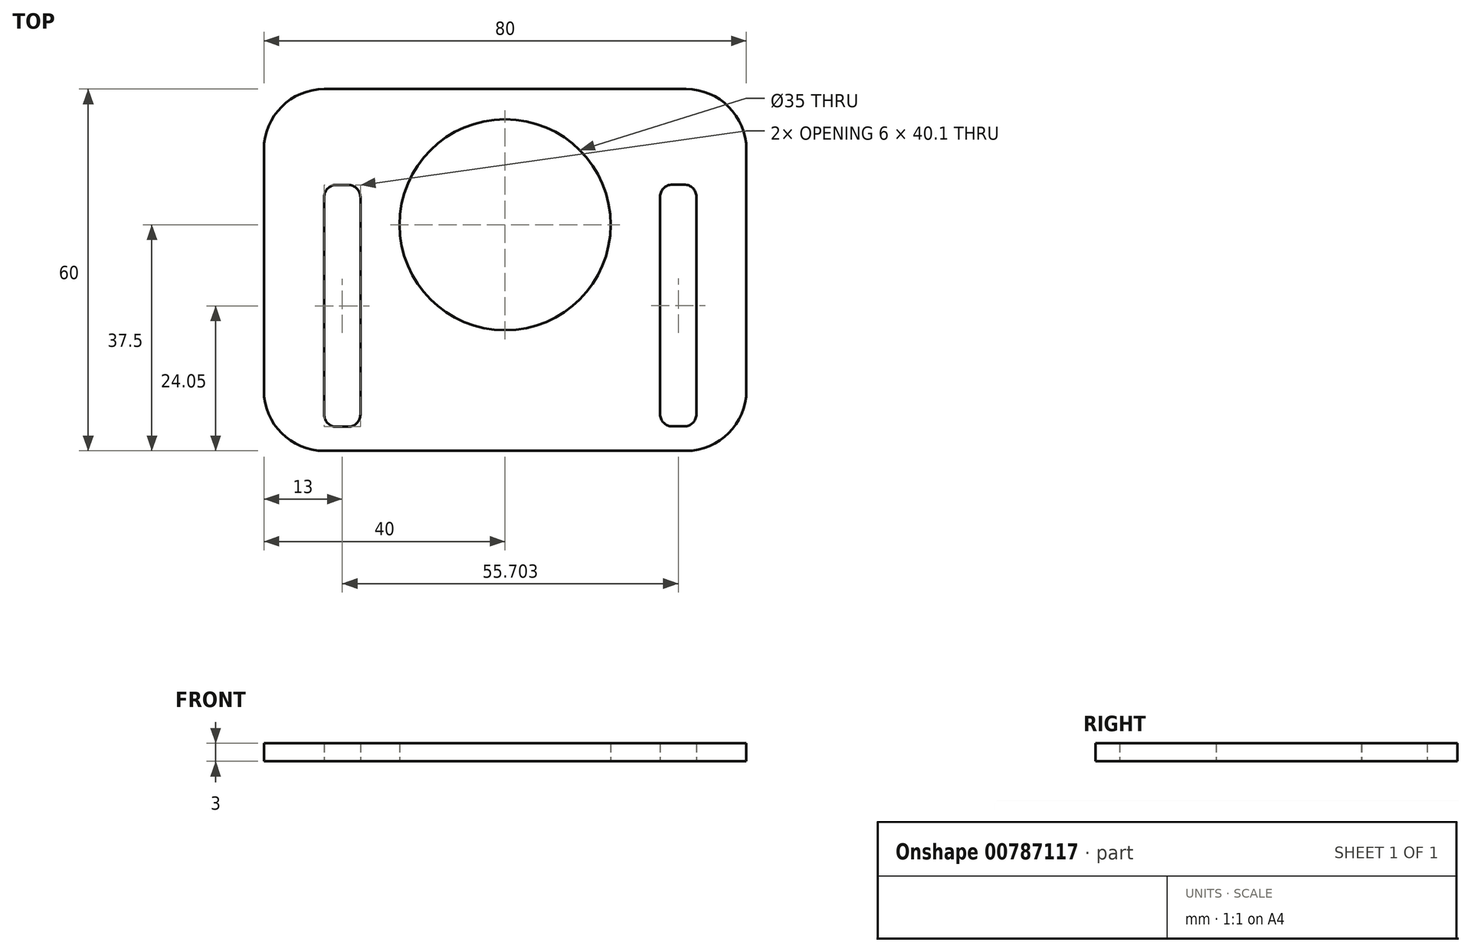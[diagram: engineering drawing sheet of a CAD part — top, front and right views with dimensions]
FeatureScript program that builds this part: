
annotation { "Feature Type Name" : "Feature", "Feature Type Description" : "" }
export const myFeature = defineFeature(function(context is Context, id is Id, definition is map)
    precondition{}
    {
        {
            var Q0;
            Q0=qCreatedBy(makeId("Top.planeOp"),FACE);
            var sketch = newSketch(context, id + "F0", { "sketchPlane" : qUnion([Q0])});
            skLineSegment(sketch, "E0.bottom", {"start": v(-10, 0) * mm, "end": v(-70, 0) * mm});
            skLineSegment(sketch, "E0.top", {"start": v(-10, 60) * mm, "end": v(-70, 60) * mm});
            skLineSegment(sketch, "E0.left", {"start": v(0, 10) * mm, "end": v(0, 50) * mm});
            skLineSegment(sketch, "E0.right", {"start": v(-80, 10) * mm, "end": v(-80, 50) * mm});
            skPoint(sketch, "E1.visualSharp", {"position": v(-80, 60) * mm});
            skArc(sketch, "E1.filletArc", {"start": v(-70, 60) * mm, "mid": v(-77.07, 57.07) * mm, "end": v(-80, 50) * mm});
            skPoint(sketch, "E2.visualSharp", {"position": v(0, 60) * mm});
            skArc(sketch, "E2.filletArc", {"start": v(0, 50) * mm, "mid": v(-2.93, 57.07) * mm, "end": v(-10, 60) * mm});
            skPoint(sketch, "E3.visualSharp", {"position": v(-80, 0) * mm});
            skArc(sketch, "E3.filletArc", {"start": v(-80, 10) * mm, "mid": v(-77.07, 2.93) * mm, "end": v(-70, 0) * mm});
            skPoint(sketch, "E4.visualSharp", {"position": v(0, 0) * mm});
            skArc(sketch, "E4.filletArc", {"start": v(-10, 0) * mm, "mid": v(-2.93, 2.93) * mm, "end": v(0, 10) * mm});
            skLineSegment(sketch, "E5", {"start": v(-40, 60) * mm, "end": v(-40, 55) * mm});
            skCircle(sketch, "E6", {"center": v(-40, 37.5) * mm, "radius": 17.5 * mm});
            skLineSegment(sketch, "E7", {"start": v(-70, 0) * mm, "end": v(-70, 4) * mm});
            skLineSegment(sketch, "E8", {"start": v(-80, 36.22) * mm, "end": v(-70.21, 36.22) * mm});
            skLineSegment(sketch, "E9.bottom", {"start": v(-68, 4) * mm, "end": v(-66, 4) * mm});
            skLineSegment(sketch, "E9.top", {"start": v(-68, 44.1) * mm, "end": v(-66, 44.1) * mm});
            skLineSegment(sketch, "E9.left", {"start": v(-70, 6) * mm, "end": v(-70, 42.1) * mm});
            skLineSegment(sketch, "E9.right", {"start": v(-64, 6) * mm, "end": v(-64, 42.1) * mm});
            skLineSegment(sketch, "E10.bottom", {"start": v(-12.3, 4.06) * mm, "end": v(-10.3, 4.06) * mm});
            skLineSegment(sketch, "E10.top", {"start": v(-12.3, 44.16) * mm, "end": v(-10.3, 44.16) * mm});
            skLineSegment(sketch, "E10.left", {"start": v(-14.3, 6.06) * mm, "end": v(-14.3, 42.16) * mm});
            skLineSegment(sketch, "E10.right", {"start": v(-8.3, 6.06) * mm, "end": v(-8.3, 42.16) * mm});
            skLineSegment(sketch, "E11", {"start": v(0, 30) * mm, "end": v(-8.4, 30) * mm});
            skLineSegment(sketch, "E12", {"start": v(-10, 0) * mm, "end": v(-10, 4) * mm});
            skPoint(sketch, "E13.visualSharp", {"position": v(-64, 46.07) * mm});
            skArc(sketch, "E13.filletArc", {"start": v(-64, 42.1) * mm, "mid": v(-64.59, 43.51) * mm, "end": v(-66, 44.1) * mm});
            skPoint(sketch, "E14.visualSharp", {"position": v(-70, 46.07) * mm});
            skArc(sketch, "E14.filletArc", {"start": v(-68, 44.1) * mm, "mid": v(-69.41, 43.51) * mm, "end": v(-70, 42.1) * mm});
            skPoint(sketch, "E15.visualSharp", {"position": v(-70, 5.97) * mm});
            skArc(sketch, "E15.filletArc", {"start": v(-70, 6) * mm, "mid": v(-69.41, 4.59) * mm, "end": v(-68, 4) * mm});
            skPoint(sketch, "E16.visualSharp", {"position": v(-64, 5.97) * mm});
            skArc(sketch, "E16.filletArc", {"start": v(-66, 4) * mm, "mid": v(-64.59, 4.59) * mm, "end": v(-64, 6) * mm});
            skPoint(sketch, "E17.visualSharp", {"position": v(-14.3, 4.06) * mm});
            skArc(sketch, "E17.filletArc", {"start": v(-14.3, 6.06) * mm, "mid": v(-13.71, 4.64) * mm, "end": v(-12.3, 4.06) * mm});
            skPoint(sketch, "E18.visualSharp", {"position": v(-8.3, 4.06) * mm});
            skArc(sketch, "E18.filletArc", {"start": v(-10.3, 4.06) * mm, "mid": v(-8.88, 4.64) * mm, "end": v(-8.3, 6.06) * mm});
            skPoint(sketch, "E19.visualSharp", {"position": v(-8.3, 44.16) * mm});
            skArc(sketch, "E19.filletArc", {"start": v(-8.3, 42.16) * mm, "mid": v(-8.88, 43.57) * mm, "end": v(-10.3, 44.16) * mm});
            skPoint(sketch, "E20.visualSharp", {"position": v(-14.3, 44.16) * mm});
            skArc(sketch, "E20.filletArc", {"start": v(-12.3, 44.16) * mm, "mid": v(-13.71, 43.57) * mm, "end": v(-14.3, 42.16) * mm});
            skLineSegment(sketch, "E21", {"start": v(-67.04, 0) * mm, "end": v(-67.04, 4) * mm});
            skSolve(sketch);
        }
        {
            var Q0;
            {var subQ9=sQuery(id+"F0.wireOp",EDGE,"E1.filletArc");Q0=makeQuery(id+"F0.imprint","IMPRINT",FACE,{"disambiguationData":[TD([[makeQuery(id+"F0.imprint","IMPRINT",EDGE,{"derivedFrom":subQ9}),1.0]])]});}
            extrude(context, id + "F1", {"entities" : qUnion([Q0]), "depth" : 3 * mm, "offsetDistance" : 25 * mm});
        }
    });
